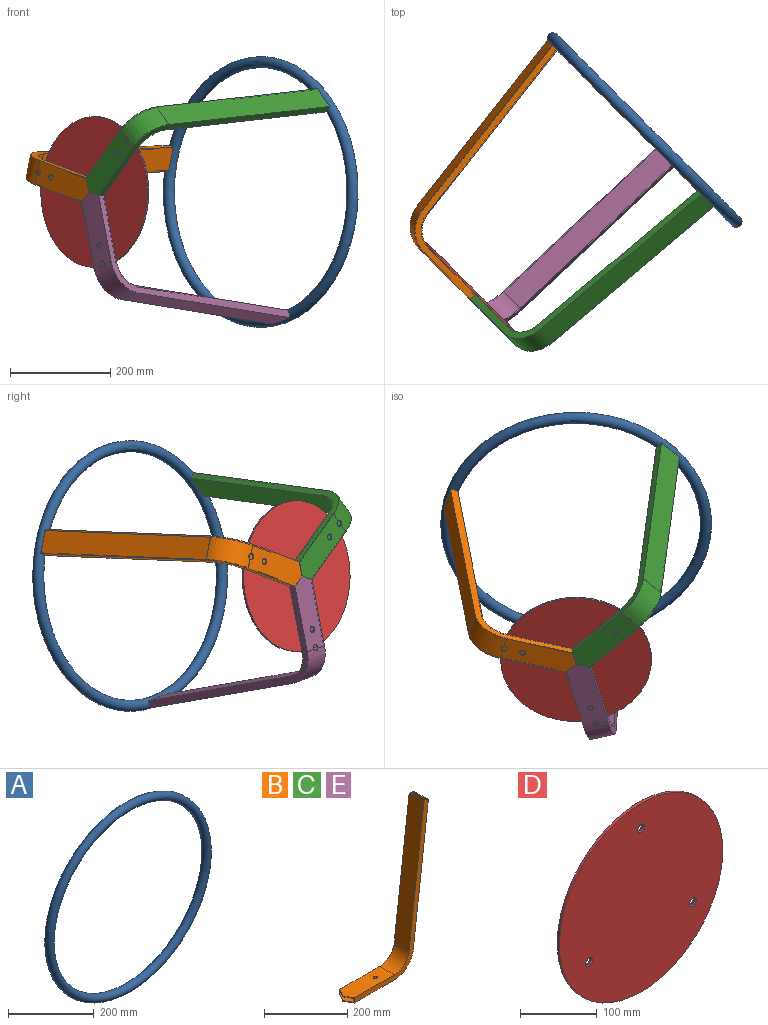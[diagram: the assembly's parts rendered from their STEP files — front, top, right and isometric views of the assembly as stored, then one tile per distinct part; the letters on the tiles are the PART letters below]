
ASSEMBLY  parts=5 mates=5
PART A: 5 faces, bbox 583.4x22x583.4 mm
  f0: torus R=258.5mm, axis (0,-1,0), area 96693.5mm2, adj f1,f2,f3
  f1: cylinder r=5mm len=10mm, axis (0,-1,0), area 50.4mm2, adj f0,f4
  f2: cylinder r=5mm len=10mm, axis (0,-1,0), area 50.4mm2, adj f0,f4
  f3: cylinder r=5mm len=10mm, axis (0,-1,0), area 50.4mm2, adj f0,f4
  f4: torus R=258.5mm, axis (0,-1,0), area 112010mm2, adj f1,f2,f3
PART B: 23 faces, bbox 265.6x50x473.2 mm
  f0: plane 150x50mm, normal (0,0,1), area 7060.6mm2, adj f5,f7,f10,f16,f17,f21
  f1: plane 150x50mm, normal (0,0,-1), area 6932.9mm2, adj f5,f8,f10,f16,f17,f19,f22
  f2: plane 150x46mm, normal (0,0,-1), area 6516mm2, adj f4,f6,f12,f16,f17,f21
  f3: plane 150x46mm, normal (0,0,1), area 6432.5mm2, adj f4,f6,f13,f16,f17,f19,f20
  f4: plane 471.17x250.31mm, normal (0,1,0), area 7021.5mm2, adj f2,f3,f12,f13,f14,f15,f17,f18
  f5: plane 473.17x251.17mm, normal (0,1,0), area 9557.4mm2, adj f0,f1,f7,f8,f9,f11,f16,f18
  f6: plane 471.17x250.31mm, normal (0,-1,0), area 7021.5mm2, adj f2,f3,f12,f13,f14,f15,f16,f18
  f7: cylinder r=50mm len=50mm, axis (0,-1,0), area 3621.6mm2, adj f0,f5,f9,f10
  f8: cylinder r=65mm len=64.52mm, axis (0,-1,0), area 4672.8mm2, adj f1,f5,f10,f11,f19
  f9: plane 414.27x50.87mm, normal (-0.99,0,0.12), area 20868.8mm2, adj f5,f7,f10,f18
  f10: plane 473.17x251.17mm, normal (0,-1,0), area 9557.4mm2, adj f0,f1,f7,f8,f9,f11,f17,f18
  f11: plane 416.09x51.09mm, normal (0.99,0,-0.12), area 20960.9mm2, adj f5,f8,f10,f18
  f12: cylinder r=52mm len=51.61mm, axis (0,-1,0), area 3465.1mm2, adj f2,f4,f6,f14
  f13: cylinder r=63mm len=62.53mm, axis (0,-1,0), area 4162.8mm2, adj f3,f4,f6,f15,f19
  f14: plane 414.51x50.9mm, normal (0.99,0,-0.12), area 19210.6mm2, adj f4,f6,f12,f18
  f15: plane 415.85x51.06mm, normal (-0.99,0,0.12), area 19272.7mm2, adj f4,f6,f13,f18
  f16: plane 25x15mm, normal (-0.87,0.5,0), area 140.9mm2, adj f0,f1,f2,f3,f5,f6,f17
  f17: plane 25x15mm, normal (-0.87,-0.5,0), area 140.9mm2, adj f0,f1,f2,f3,f4,f10,f16
  f18: plane 50x15.11mm, normal (0,0,1), area 245.8mm2, adj f4,f5,f6,f9,f10,f11,f14,f15
  f19: cylinder r=6.15mm len=12.3mm, axis (0,0,-1), area 77.3mm2, adj f1,f3,f8,f13
  f20: cylinder r=5mm len=10mm, axis (0,0,1), area 23.6mm2, adj f3,f22
  f21: cylinder r=5mm len=10mm, axis (0,0,1), area 62.8mm2, adj f0,f2
  f22: cone r=5mm half-angle=45deg, axis (0,0,-1), area 62.5mm2, adj f1,f20
PART C: same geometry as B
PART D: 9 faces, bbox 300x4x300 mm
  f0: cylinder r=4.5mm len=9mm, axis (0,1,0), area 56.5mm2, adj f5,f8
  f1: cylinder r=4.5mm len=9mm, axis (0,1,0), area 56.5mm2, adj f5,f6
  f2: cylinder r=4.5mm len=9mm, axis (0,1,0), area 56.5mm2, adj f5,f7
  f3: cylinder r=150mm len=300mm, axis (0,1,0), area 3769.9mm2, adj f4,f5
  f4: plane 300x300mm, normal (0,-1,0), area 70287.6mm2, adj f3,f6,f7,f8
  f5: plane 300x300mm, normal (0,1,0), area 70495mm2, adj f0,f1,f2,f3
  f6: cone r=4.5mm half-angle=45deg, axis (0,-1,0), area 97.7mm2, adj f1,f4
  f7: cone r=4.5mm half-angle=45deg, axis (0,-1,0), area 97.7mm2, adj f2,f4
  f8: cone r=4.5mm half-angle=45deg, axis (0,-1,0), area 97.7mm2, adj f0,f4
PART E: same geometry as B
PLACE A rot(axis=(-0.21,-0.5,-0.84),52.3deg) t=(-29.02,132.47,-215.22)mm
PLACE B rot(axis=(0.36,0.62,0.69),158.9deg) t=(-356.22,-203.88,-191.07)mm
PLACE C rot(axis=(-0.82,0,-0.58),120deg) t=(-348.3,-211.81,-232.9)mm
PLACE D rot(axis=(0.92,-0.38,0.12),174.3deg) t=(-360.8,-199.31,-215.22)mm
PLACE E rot(axis=(-0.48,0.84,0.25),93.8deg) t=(-377.87,-182.23,-221.69)mm
MATE cylindrical D.f2 <-> C.f20  axis (0.71,0.71,0) through (-302.97,-251.48,-137.44)mm
MATE planar D.f3 <-> A.f0  axis (0.71,0.71,0) through (-357.97,-196.48,-215.22)mm
MATE cylindrical D.f1 <-> B.f20  axis (0.71,0.71,0) through (-433.1,-121.35,-186.75)mm
MATE planar D.f3 <-> E.f0  axis (-0.71,-0.71,0) through (-360.8,-199.31,-215.22)mm
MATE cylindrical D.f3 <-> A.f0  axis (0.71,0.71,0) through (-357.97,-196.48,-215.22)mm
